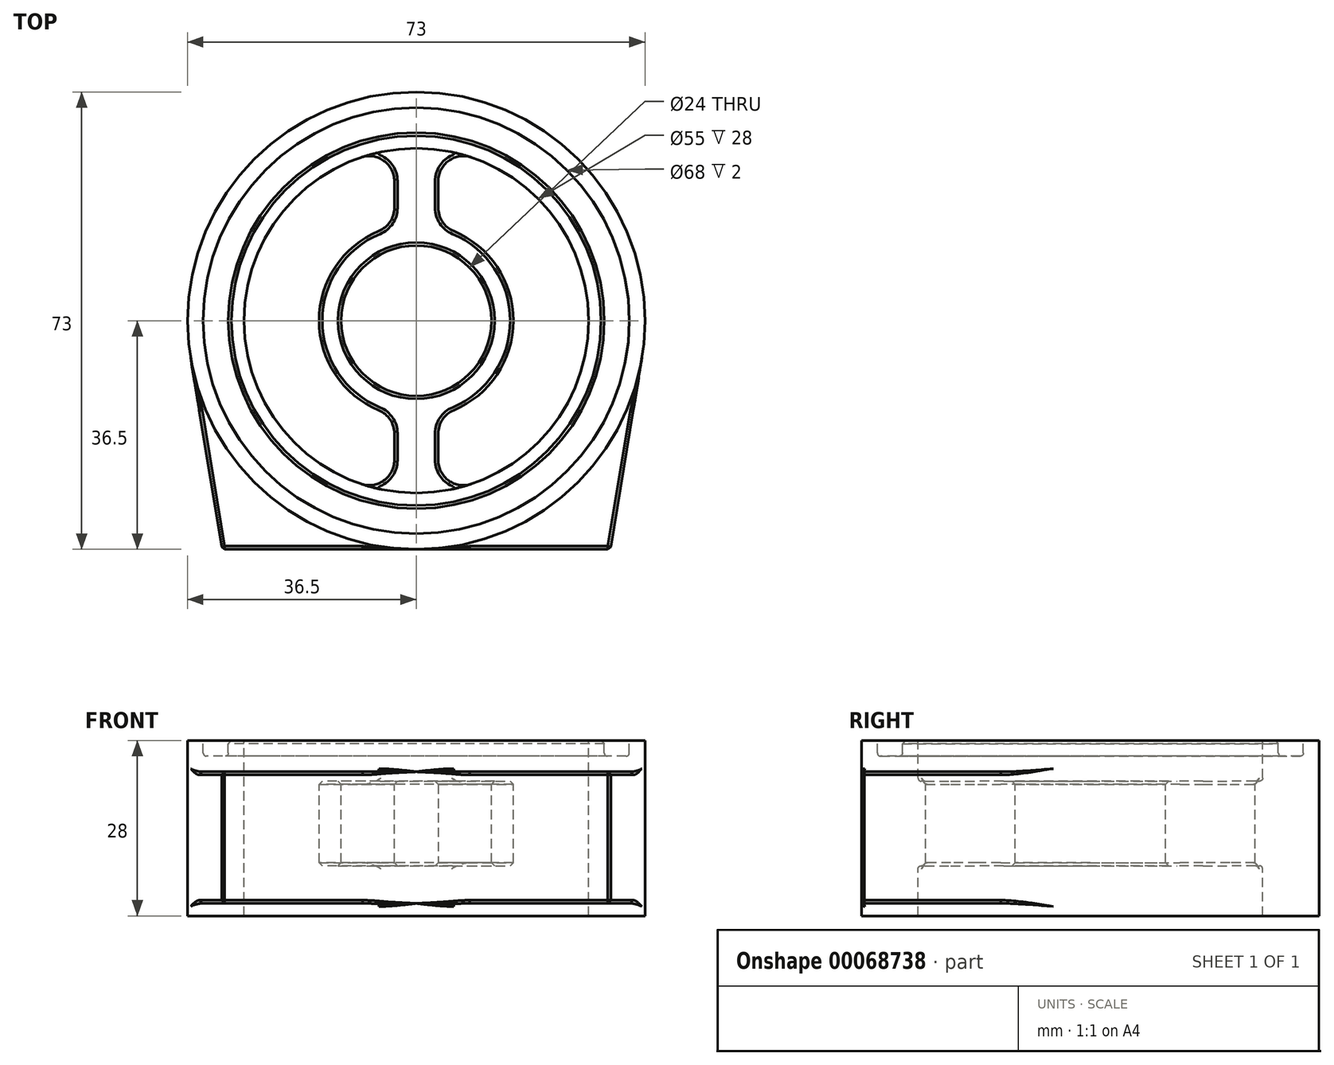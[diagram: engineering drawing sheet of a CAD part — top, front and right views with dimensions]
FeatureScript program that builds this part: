
annotation { "Feature Type Name" : "Feature", "Feature Type Description" : "" }
export const myFeature = defineFeature(function(context is Context, id is Id, definition is map)
    precondition{}
    {
        {
            var Q0;
            Q0=qCreatedBy(makeId("Top.planeOp"),FACE);
            var sketch = newSketch(context, id + "F0", { "sketchPlane" : qUnion([Q0])});
            skCircle(sketch, "E0", {"center": v(0, 0) * mm, "radius": 36.5 * mm});
            skLineSegment(sketch, "E1", {"start": v(-70.7, 0) * mm, "end": v(75.45, 0) * mm, "construction": true});
            skLineSegment(sketch, "E2", {"start": v(0, 57.55) * mm, "end": v(0, -65.93) * mm, "construction": true});
            skLineSegment(sketch, "E3", {"start": v(-31, -36.5) * mm, "end": v(31, -36.5) * mm});
            skLineSegment(sketch, "E4", {"start": v(31, -36.5) * mm, "end": v(36.02, -5.9) * mm});
            skLineSegment(sketch, "E5", {"start": v(-31, -36.5) * mm, "end": v(-36.02, -5.9) * mm});
            skSolve(sketch);
        }
        {
            var Q0;
            Q0 = qSketchRegion(id + "F0", true);
            extrude(context, id + "F1", {"entities" : qUnion([Q0]), "endBound" : BoundingType.SYMMETRIC, "depth" : 28 * mm});
        }
        {
            var Q0;
            Q0=makeQuery(id+"F1.opExtrude","CAP_FACE",FACE,{"disambiguationData":[OSD([sQuery(id+"F0.wireOp",EDGE,"E0"),sQuery(id+"F0.wireOp",EDGE,"E3"),sQuery(id+"F0.wireOp",EDGE,"E4"),sQuery(id+"F0.wireOp",EDGE,"E5")])],"isStart":false});
            var sketch = newSketch(context, id + "F2", { "sketchPlane" : qUnion([Q0])});
            skLineSegment(sketch, "E6", {"start": v(-31, -36.5) * mm, "end": v(-36.02, -5.9) * mm});
            skLineSegment(sketch, "E7", {"start": v(31, -36.5) * mm, "end": v(36.02, -5.9) * mm});
            skLineSegment(sketch, "E8", {"start": v(-31, -36.5) * mm, "end": v(31, -36.5) * mm});
            skArc(sketch, "E9", {"start": v(-36.02, -5.9) * mm, "mid": v(0, -36.5) * mm, "end": v(36.02, -5.9) * mm});
            skSolve(sketch);
        }
        {
            var Q0;
            Q0 = qSketchRegion(id + "F2", true);
            extrude(context, id + "F3", {"entities" : qUnion([Q0]), "operationType" : NewBodyOperationType.REMOVE, "oppositeDirection" : true, "depth" : 5 * mm});
        }
        {
            var Q0;
            Q0=makeQuery(id+"F1.opExtrude","CAP_FACE",FACE,{"disambiguationData":[OSD([sQuery(id+"F0.wireOp",EDGE,"E0"),sQuery(id+"F0.wireOp",EDGE,"E3"),sQuery(id+"F0.wireOp",EDGE,"E4"),sQuery(id+"F0.wireOp",EDGE,"E5")])],"isStart":true});
            var sketch = newSketch(context, id + "F4", { "sketchPlane" : qUnion([Q0])});
            skArc(sketch, "E10", {"start": v(36.02, 5.9) * mm, "mid": v(0, 36.5) * mm, "end": v(-36.02, 5.9) * mm});
            skLineSegment(sketch, "E11", {"start": v(-31, 36.5) * mm, "end": v(31, 36.5) * mm});
            skLineSegment(sketch, "E12", {"start": v(31, 36.5) * mm, "end": v(36.02, 5.9) * mm});
            skLineSegment(sketch, "E13", {"start": v(-31, 36.5) * mm, "end": v(-36.02, 5.9) * mm});
            skSolve(sketch);
        }
        {
            var Q0;
            Q0 = qSketchRegion(id + "F4", true);
            extrude(context, id + "F5", {"entities" : qUnion([Q0]), "operationType" : NewBodyOperationType.REMOVE, "oppositeDirection" : true, "depth" : 2 * mm});
        }
        {
            var Q0;
            Q0=makeQuery(id+"F1.opExtrude","CAP_FACE",FACE,{"disambiguationData":[OSD([sQuery(id+"F0.wireOp",EDGE,"E0"),sQuery(id+"F0.wireOp",EDGE,"E3"),sQuery(id+"F0.wireOp",EDGE,"E4"),sQuery(id+"F0.wireOp",EDGE,"E5")])],"isStart":false});
            var sketch = newSketch(context, id + "F6", { "sketchPlane" : qUnion([Q0])});
            skArc(sketch, "E14", {"start": v(-3.5, 27.28) * mm, "mid": v(-27.5, 0) * mm, "end": v(-3.5, -27.28) * mm});
            skArc(sketch, "E15", {"start": v(-3.5, 15.1) * mm, "mid": v(-15.5, 0) * mm, "end": v(-3.5, -15.1) * mm});
            skCircle(sketch, "E16", {"center": v(0, 0) * mm, "radius": 12 * mm});
            skLineSegment(sketch, "E17", {"start": v(-3.5, 27.28) * mm, "end": v(-3.5, 15.1) * mm});
            skLineSegment(sketch, "E18", {"start": v(3.5, 27.28) * mm, "end": v(3.5, 15.1) * mm});
            skLineSegment(sketch, "E19", {"start": v(-3.5, -15.1) * mm, "end": v(-3.5, -27.28) * mm});
            skLineSegment(sketch, "E20", {"start": v(3.5, -15.1) * mm, "end": v(3.5, -27.28) * mm});
            skArc(sketch, "E21.trimOffspring", {"start": v(3.5, -15.1) * mm, "mid": v(15.5, 0) * mm, "end": v(3.5, 15.1) * mm});
            skArc(sketch, "E22.trimOffspring", {"start": v(3.5, -27.28) * mm, "mid": v(27.5, 0) * mm, "end": v(3.5, 27.28) * mm});
            skSolve(sketch);
        }
        {
            var Q0;
            Q0 = qSketchRegion(id + "F6", true);
            extrude(context, id + "F7", {"entities" : qUnion([Q0]), "operationType" : NewBodyOperationType.REMOVE, "endBound" : BoundingType.THROUGH_ALL, "oppositeDirection" : true, "depth" : 25 * mm});
        }
        {
            var Q0;
            Q0=makeQuery(id+"F7.boolean.opBoolean","COPY",EDGE,{"derivedFrom":makeQuery(id+"F7.opExtrude","SWEPT_EDGE",EDGE,{"disambiguationData":[OSD([sQuery(id+"F6.wireOp",EDGE,"E18"),sQuery(id+"F6.wireOp",EDGE,"E22.trimOffspring")])]})});
            var Q1;
            Q1=makeQuery(id+"F7.boolean.opBoolean","COPY",EDGE,{"derivedFrom":makeQuery(id+"F7.opExtrude","SWEPT_EDGE",EDGE,{"disambiguationData":[OSD([sQuery(id+"F6.wireOp",EDGE,"E18"),sQuery(id+"F6.wireOp",EDGE,"E21.trimOffspring")])]})});
            var Q2;
            Q2=makeQuery(id+"F7.boolean.opBoolean","COPY",EDGE,{"derivedFrom":makeQuery(id+"F7.opExtrude","SWEPT_EDGE",EDGE,{"disambiguationData":[OSD([sQuery(id+"F6.wireOp",EDGE,"E20"),sQuery(id+"F6.wireOp",EDGE,"E21.trimOffspring")])]})});
            var Q3;
            Q3=makeQuery(id+"F7.boolean.opBoolean","COPY",EDGE,{"derivedFrom":makeQuery(id+"F7.opExtrude","SWEPT_EDGE",EDGE,{"disambiguationData":[OSD([sQuery(id+"F6.wireOp",EDGE,"E20"),sQuery(id+"F6.wireOp",EDGE,"E22.trimOffspring")])]})});
            var Q4;
            Q4=makeQuery(id+"F7.boolean.opBoolean","COPY",EDGE,{"derivedFrom":makeQuery(id+"F7.opExtrude","SWEPT_EDGE",EDGE,{"disambiguationData":[OSD([sQuery(id+"F6.wireOp",EDGE,"E14"),sQuery(id+"F6.wireOp",EDGE,"E17")])]})});
            var Q5;
            Q5=makeQuery(id+"F7.boolean.opBoolean","COPY",EDGE,{"derivedFrom":makeQuery(id+"F7.opExtrude","SWEPT_EDGE",EDGE,{"disambiguationData":[OSD([sQuery(id+"F6.wireOp",EDGE,"E15"),sQuery(id+"F6.wireOp",EDGE,"E17")])]})});
            var Q6;
            Q6=makeQuery(id+"F7.boolean.opBoolean","COPY",EDGE,{"derivedFrom":makeQuery(id+"F7.opExtrude","SWEPT_EDGE",EDGE,{"disambiguationData":[OSD([sQuery(id+"F6.wireOp",EDGE,"E15"),sQuery(id+"F6.wireOp",EDGE,"E19")])]})});
            var Q7;
            Q7=makeQuery(id+"F7.boolean.opBoolean","COPY",EDGE,{"derivedFrom":makeQuery(id+"F7.opExtrude","SWEPT_EDGE",EDGE,{"disambiguationData":[OSD([sQuery(id+"F6.wireOp",EDGE,"E14"),sQuery(id+"F6.wireOp",EDGE,"E19")])]})});
            fillet(context, id + "F8", {"entities" : qUnion([Q0, Q1, Q2, Q3, Q4, Q5, Q6, Q7]), "radius" : 4 * mm, "tangentPropagation" : true, "allowEdgeOverflow" : false});
        }
        {
            var Q0;
            Q0=makeQuery(id+"F1.opExtrude","CAP_FACE",FACE,{"disambiguationData":[OSD([sQuery(id+"F0.wireOp",EDGE,"E0"),sQuery(id+"F0.wireOp",EDGE,"E3"),sQuery(id+"F0.wireOp",EDGE,"E4"),sQuery(id+"F0.wireOp",EDGE,"E5")])],"isStart":false});
            var sketch = newSketch(context, id + "F9", { "sketchPlane" : qUnion([Q0])});
            skCircle(sketch, "E23", {"center": v(0, 0) * mm, "radius": 27.5 * mm});
            skSolve(sketch);
        }
        {
            var Q0;
            Q0 = qSketchRegion(id + "F9", true);
            extrude(context, id + "F10", {"entities" : qUnion([Q0]), "operationType" : NewBodyOperationType.REMOVE, "oppositeDirection" : true, "depth" : 6.5 * mm});
        }
        {
            var Q0;
            Q0=makeQuery(id+"F1.opExtrude","CAP_FACE",FACE,{"disambiguationData":[OSD([sQuery(id+"F0.wireOp",EDGE,"E0"),sQuery(id+"F0.wireOp",EDGE,"E3"),sQuery(id+"F0.wireOp",EDGE,"E4"),sQuery(id+"F0.wireOp",EDGE,"E5")])],"isStart":true});
            var sketch = newSketch(context, id + "F11", { "sketchPlane" : qUnion([Q0])});
            skCircle(sketch, "E24", {"center": v(0, 0) * mm, "radius": 27.5 * mm});
            skSolve(sketch);
        }
        {
            var Q0;
            Q0 = qSketchRegion(id + "F11", true);
            extrude(context, id + "F12", {"entities" : qUnion([Q0]), "operationType" : NewBodyOperationType.REMOVE, "oppositeDirection" : true, "depth" : 8 * mm});
        }
        {
            var Q0;
            Q0=makeQuery(id+"F1.opExtrude","CAP_FACE",FACE,{"disambiguationData":[OSD([sQuery(id+"F0.wireOp",EDGE,"E0"),sQuery(id+"F0.wireOp",EDGE,"E3"),sQuery(id+"F0.wireOp",EDGE,"E4"),sQuery(id+"F0.wireOp",EDGE,"E5")])],"isStart":false});
            var sketch = newSketch(context, id + "F13", { "sketchPlane" : qUnion([Q0])});
            skCircle(sketch, "E25", {"center": v(0, 0) * mm, "radius": 30 * mm});
            skCircle(sketch, "E26", {"center": v(0, 0) * mm, "radius": 34 * mm});
            skSolve(sketch);
        }
        {
            var Q0;
            Q0 = qSketchRegion(id + "F13", true);
            extrude(context, id + "F14", {"entities" : qUnion([Q0]), "operationType" : NewBodyOperationType.REMOVE, "oppositeDirection" : true, "depth" : 2.5 * mm});
        }
        {
            var Q0;
            Q0=makeQuery(id+"F10.boolean.opBoolean","INTERSECT",EDGE,{"derivedFrom":[makeQuery(id+"F8.opFillet","BLEND_FACE",FACE,{"disambiguationData":[OSD([sQuery(id+"F6.wireOp",EDGE,"E18"),sQuery(id+"F6.wireOp",EDGE,"E22.trimOffspring")])]}),makeQuery(id+"F10.opExtrude","CAP_FACE",FACE,{"disambiguationData":[OSD([sQuery(id+"F9.wireOp",EDGE,"E23")])],"isStart":false})]});
            var Q1;
            Q1=makeQuery(id+"F10.boolean.opBoolean","INTERSECT",EDGE,{"derivedFrom":[makeQuery(id+"F7.boolean.opBoolean","COPY",FACE,{"derivedFrom":makeQuery(id+"F7.opExtrude","SWEPT_FACE",FACE,{"disambiguationData":[OSD([sQuery(id+"F6.wireOp",EDGE,"E18")])]})}),makeQuery(id+"F10.opExtrude","CAP_FACE",FACE,{"disambiguationData":[OSD([sQuery(id+"F9.wireOp",EDGE,"E23")])],"isStart":false})]});
            var Q2;
            Q2=makeQuery(id+"F10.boolean.opBoolean","INTERSECT",EDGE,{"derivedFrom":[makeQuery(id+"F8.opFillet","BLEND_FACE",FACE,{"disambiguationData":[OSD([sQuery(id+"F6.wireOp",EDGE,"E18"),sQuery(id+"F6.wireOp",EDGE,"E21.trimOffspring")])]}),makeQuery(id+"F10.opExtrude","CAP_FACE",FACE,{"disambiguationData":[OSD([sQuery(id+"F9.wireOp",EDGE,"E23")])],"isStart":false})]});
            var Q3;
            Q3=makeQuery(id+"F10.boolean.opBoolean","INTERSECT",EDGE,{"derivedFrom":[makeQuery(id+"F7.boolean.opBoolean","COPY",FACE,{"derivedFrom":makeQuery(id+"F7.opExtrude","SWEPT_FACE",FACE,{"disambiguationData":[OSD([sQuery(id+"F6.wireOp",EDGE,"E21.trimOffspring")])]})}),makeQuery(id+"F10.opExtrude","CAP_FACE",FACE,{"disambiguationData":[OSD([sQuery(id+"F9.wireOp",EDGE,"E23")])],"isStart":false})]});
            var Q4;
            Q4=makeQuery(id+"F10.boolean.opBoolean","INTERSECT",EDGE,{"derivedFrom":[makeQuery(id+"F8.opFillet","BLEND_FACE",FACE,{"disambiguationData":[OSD([sQuery(id+"F6.wireOp",EDGE,"E20"),sQuery(id+"F6.wireOp",EDGE,"E21.trimOffspring")])]}),makeQuery(id+"F10.opExtrude","CAP_FACE",FACE,{"disambiguationData":[OSD([sQuery(id+"F9.wireOp",EDGE,"E23")])],"isStart":false})]});
            var Q5;
            Q5=makeQuery(id+"F10.boolean.opBoolean","INTERSECT",EDGE,{"derivedFrom":[makeQuery(id+"F7.boolean.opBoolean","COPY",FACE,{"derivedFrom":makeQuery(id+"F7.opExtrude","SWEPT_FACE",FACE,{"disambiguationData":[OSD([sQuery(id+"F6.wireOp",EDGE,"E20")])]})}),makeQuery(id+"F10.opExtrude","CAP_FACE",FACE,{"disambiguationData":[OSD([sQuery(id+"F9.wireOp",EDGE,"E23")])],"isStart":false})]});
            var Q6;
            Q6=makeQuery(id+"F10.boolean.opBoolean","INTERSECT",EDGE,{"derivedFrom":[makeQuery(id+"F8.opFillet","BLEND_FACE",FACE,{"disambiguationData":[OSD([sQuery(id+"F6.wireOp",EDGE,"E20"),sQuery(id+"F6.wireOp",EDGE,"E22.trimOffspring")])]}),makeQuery(id+"F10.opExtrude","CAP_FACE",FACE,{"disambiguationData":[OSD([sQuery(id+"F9.wireOp",EDGE,"E23")])],"isStart":false})]});
            var Q7;
            Q7=makeQuery(id+"F10.boolean.opBoolean","INTERSECT",EDGE,{"derivedFrom":[makeQuery(id+"F8.opFillet","BLEND_FACE",FACE,{"disambiguationData":[OSD([sQuery(id+"F6.wireOp",EDGE,"E14"),sQuery(id+"F6.wireOp",EDGE,"E19")])]}),makeQuery(id+"F10.opExtrude","CAP_FACE",FACE,{"disambiguationData":[OSD([sQuery(id+"F9.wireOp",EDGE,"E23")])],"isStart":false})]});
            var Q8;
            Q8=makeQuery(id+"F10.boolean.opBoolean","INTERSECT",EDGE,{"derivedFrom":[makeQuery(id+"F7.boolean.opBoolean","COPY",FACE,{"derivedFrom":makeQuery(id+"F7.opExtrude","SWEPT_FACE",FACE,{"disambiguationData":[OSD([sQuery(id+"F6.wireOp",EDGE,"E19")])]})}),makeQuery(id+"F10.opExtrude","CAP_FACE",FACE,{"disambiguationData":[OSD([sQuery(id+"F9.wireOp",EDGE,"E23")])],"isStart":false})]});
            var Q9;
            Q9=makeQuery(id+"F10.boolean.opBoolean","INTERSECT",EDGE,{"derivedFrom":[makeQuery(id+"F8.opFillet","BLEND_FACE",FACE,{"disambiguationData":[OSD([sQuery(id+"F6.wireOp",EDGE,"E15"),sQuery(id+"F6.wireOp",EDGE,"E19")])]}),makeQuery(id+"F10.opExtrude","CAP_FACE",FACE,{"disambiguationData":[OSD([sQuery(id+"F9.wireOp",EDGE,"E23")])],"isStart":false})]});
            var Q10;
            Q10=makeQuery(id+"F10.boolean.opBoolean","INTERSECT",EDGE,{"derivedFrom":[makeQuery(id+"F7.boolean.opBoolean","COPY",FACE,{"derivedFrom":makeQuery(id+"F7.opExtrude","SWEPT_FACE",FACE,{"disambiguationData":[OSD([sQuery(id+"F6.wireOp",EDGE,"E15")])]})}),makeQuery(id+"F10.opExtrude","CAP_FACE",FACE,{"disambiguationData":[OSD([sQuery(id+"F9.wireOp",EDGE,"E23")])],"isStart":false})]});
            var Q11;
            Q11=makeQuery(id+"F10.boolean.opBoolean","INTERSECT",EDGE,{"derivedFrom":[makeQuery(id+"F8.opFillet","BLEND_FACE",FACE,{"disambiguationData":[OSD([sQuery(id+"F6.wireOp",EDGE,"E15"),sQuery(id+"F6.wireOp",EDGE,"E17")])]}),makeQuery(id+"F10.opExtrude","CAP_FACE",FACE,{"disambiguationData":[OSD([sQuery(id+"F9.wireOp",EDGE,"E23")])],"isStart":false})]});
            var Q12;
            Q12=makeQuery(id+"F10.boolean.opBoolean","INTERSECT",EDGE,{"derivedFrom":[makeQuery(id+"F7.boolean.opBoolean","COPY",FACE,{"derivedFrom":makeQuery(id+"F7.opExtrude","SWEPT_FACE",FACE,{"disambiguationData":[OSD([sQuery(id+"F6.wireOp",EDGE,"E17")])]})}),makeQuery(id+"F10.opExtrude","CAP_FACE",FACE,{"disambiguationData":[OSD([sQuery(id+"F9.wireOp",EDGE,"E23")])],"isStart":false})]});
            var Q13;
            Q13=makeQuery(id+"F10.boolean.opBoolean","INTERSECT",EDGE,{"derivedFrom":[makeQuery(id+"F8.opFillet","BLEND_FACE",FACE,{"disambiguationData":[OSD([sQuery(id+"F6.wireOp",EDGE,"E14"),sQuery(id+"F6.wireOp",EDGE,"E17")])]}),makeQuery(id+"F10.opExtrude","CAP_FACE",FACE,{"disambiguationData":[OSD([sQuery(id+"F9.wireOp",EDGE,"E23")])],"isStart":false})]});
            var Q14;
            Q14=makeQuery(id+"F10.boolean.opBoolean","INTERSECT",EDGE,{"derivedFrom":[makeQuery(id+"F7.boolean.opBoolean","COPY",FACE,{"derivedFrom":makeQuery(id+"F7.opExtrude","SWEPT_FACE",FACE,{"disambiguationData":[OSD([sQuery(id+"F6.wireOp",EDGE,"E16")])]})}),makeQuery(id+"F10.opExtrude","CAP_FACE",FACE,{"disambiguationData":[OSD([sQuery(id+"F9.wireOp",EDGE,"E23")])],"isStart":false})]});
            var Q15;
            Q15=makeQuery(id+"F12.boolean.opBoolean","INTERSECT",EDGE,{"derivedFrom":[makeQuery(id+"F8.opFillet","BLEND_FACE",FACE,{"disambiguationData":[OSD([sQuery(id+"F6.wireOp",EDGE,"E18"),sQuery(id+"F6.wireOp",EDGE,"E22.trimOffspring")])]}),makeQuery(id+"F12.opExtrude","CAP_FACE",FACE,{"disambiguationData":[OSD([sQuery(id+"F11.wireOp",EDGE,"E24")])],"isStart":false})]});
            var Q16;
            Q16=makeQuery(id+"F12.boolean.opBoolean","INTERSECT",EDGE,{"derivedFrom":[makeQuery(id+"F7.boolean.opBoolean","COPY",FACE,{"derivedFrom":makeQuery(id+"F7.opExtrude","SWEPT_FACE",FACE,{"disambiguationData":[OSD([sQuery(id+"F6.wireOp",EDGE,"E18")])]})}),makeQuery(id+"F12.opExtrude","CAP_FACE",FACE,{"disambiguationData":[OSD([sQuery(id+"F11.wireOp",EDGE,"E24")])],"isStart":false})]});
            var Q17;
            Q17=makeQuery(id+"F12.boolean.opBoolean","INTERSECT",EDGE,{"derivedFrom":[makeQuery(id+"F8.opFillet","BLEND_FACE",FACE,{"disambiguationData":[OSD([sQuery(id+"F6.wireOp",EDGE,"E18"),sQuery(id+"F6.wireOp",EDGE,"E21.trimOffspring")])]}),makeQuery(id+"F12.opExtrude","CAP_FACE",FACE,{"disambiguationData":[OSD([sQuery(id+"F11.wireOp",EDGE,"E24")])],"isStart":false})]});
            var Q18;
            Q18=makeQuery(id+"F12.boolean.opBoolean","INTERSECT",EDGE,{"derivedFrom":[makeQuery(id+"F7.boolean.opBoolean","COPY",FACE,{"derivedFrom":makeQuery(id+"F7.opExtrude","SWEPT_FACE",FACE,{"disambiguationData":[OSD([sQuery(id+"F6.wireOp",EDGE,"E21.trimOffspring")])]})}),makeQuery(id+"F12.opExtrude","CAP_FACE",FACE,{"disambiguationData":[OSD([sQuery(id+"F11.wireOp",EDGE,"E24")])],"isStart":false})]});
            var Q19;
            Q19=makeQuery(id+"F12.boolean.opBoolean","INTERSECT",EDGE,{"derivedFrom":[makeQuery(id+"F8.opFillet","BLEND_FACE",FACE,{"disambiguationData":[OSD([sQuery(id+"F6.wireOp",EDGE,"E20"),sQuery(id+"F6.wireOp",EDGE,"E21.trimOffspring")])]}),makeQuery(id+"F12.opExtrude","CAP_FACE",FACE,{"disambiguationData":[OSD([sQuery(id+"F11.wireOp",EDGE,"E24")])],"isStart":false})]});
            var Q20;
            Q20=makeQuery(id+"F12.boolean.opBoolean","INTERSECT",EDGE,{"derivedFrom":[makeQuery(id+"F7.boolean.opBoolean","COPY",FACE,{"derivedFrom":makeQuery(id+"F7.opExtrude","SWEPT_FACE",FACE,{"disambiguationData":[OSD([sQuery(id+"F6.wireOp",EDGE,"E20")])]})}),makeQuery(id+"F12.opExtrude","CAP_FACE",FACE,{"disambiguationData":[OSD([sQuery(id+"F11.wireOp",EDGE,"E24")])],"isStart":false})]});
            var Q21;
            Q21=makeQuery(id+"F12.boolean.opBoolean","INTERSECT",EDGE,{"derivedFrom":[makeQuery(id+"F8.opFillet","BLEND_FACE",FACE,{"disambiguationData":[OSD([sQuery(id+"F6.wireOp",EDGE,"E20"),sQuery(id+"F6.wireOp",EDGE,"E22.trimOffspring")])]}),makeQuery(id+"F12.opExtrude","CAP_FACE",FACE,{"disambiguationData":[OSD([sQuery(id+"F11.wireOp",EDGE,"E24")])],"isStart":false})]});
            var Q22;
            Q22=makeQuery(id+"F12.boolean.opBoolean","INTERSECT",EDGE,{"derivedFrom":[makeQuery(id+"F7.boolean.opBoolean","COPY",FACE,{"derivedFrom":makeQuery(id+"F7.opExtrude","SWEPT_FACE",FACE,{"disambiguationData":[OSD([sQuery(id+"F6.wireOp",EDGE,"E16")])]})}),makeQuery(id+"F12.opExtrude","CAP_FACE",FACE,{"disambiguationData":[OSD([sQuery(id+"F11.wireOp",EDGE,"E24")])],"isStart":false})]});
            var Q23;
            Q23=makeQuery(id+"F12.boolean.opBoolean","INTERSECT",EDGE,{"derivedFrom":[makeQuery(id+"F8.opFillet","BLEND_FACE",FACE,{"disambiguationData":[OSD([sQuery(id+"F6.wireOp",EDGE,"E14"),sQuery(id+"F6.wireOp",EDGE,"E17")])]}),makeQuery(id+"F12.opExtrude","CAP_FACE",FACE,{"disambiguationData":[OSD([sQuery(id+"F11.wireOp",EDGE,"E24")])],"isStart":false})]});
            var Q24;
            Q24=makeQuery(id+"F12.boolean.opBoolean","INTERSECT",EDGE,{"derivedFrom":[makeQuery(id+"F7.boolean.opBoolean","COPY",FACE,{"derivedFrom":makeQuery(id+"F7.opExtrude","SWEPT_FACE",FACE,{"disambiguationData":[OSD([sQuery(id+"F6.wireOp",EDGE,"E17")])]})}),makeQuery(id+"F12.opExtrude","CAP_FACE",FACE,{"disambiguationData":[OSD([sQuery(id+"F11.wireOp",EDGE,"E24")])],"isStart":false})]});
            var Q25;
            Q25=makeQuery(id+"F12.boolean.opBoolean","INTERSECT",EDGE,{"derivedFrom":[makeQuery(id+"F8.opFillet","BLEND_FACE",FACE,{"disambiguationData":[OSD([sQuery(id+"F6.wireOp",EDGE,"E15"),sQuery(id+"F6.wireOp",EDGE,"E17")])]}),makeQuery(id+"F12.opExtrude","CAP_FACE",FACE,{"disambiguationData":[OSD([sQuery(id+"F11.wireOp",EDGE,"E24")])],"isStart":false})]});
            var Q26;
            Q26=makeQuery(id+"F12.boolean.opBoolean","INTERSECT",EDGE,{"derivedFrom":[makeQuery(id+"F7.boolean.opBoolean","COPY",FACE,{"derivedFrom":makeQuery(id+"F7.opExtrude","SWEPT_FACE",FACE,{"disambiguationData":[OSD([sQuery(id+"F6.wireOp",EDGE,"E15")])]})}),makeQuery(id+"F12.opExtrude","CAP_FACE",FACE,{"disambiguationData":[OSD([sQuery(id+"F11.wireOp",EDGE,"E24")])],"isStart":false})]});
            var Q27;
            Q27=makeQuery(id+"F12.boolean.opBoolean","INTERSECT",EDGE,{"derivedFrom":[makeQuery(id+"F8.opFillet","BLEND_FACE",FACE,{"disambiguationData":[OSD([sQuery(id+"F6.wireOp",EDGE,"E15"),sQuery(id+"F6.wireOp",EDGE,"E19")])]}),makeQuery(id+"F12.opExtrude","CAP_FACE",FACE,{"disambiguationData":[OSD([sQuery(id+"F11.wireOp",EDGE,"E24")])],"isStart":false})]});
            var Q28;
            Q28=makeQuery(id+"F12.boolean.opBoolean","INTERSECT",EDGE,{"derivedFrom":[makeQuery(id+"F7.boolean.opBoolean","COPY",FACE,{"derivedFrom":makeQuery(id+"F7.opExtrude","SWEPT_FACE",FACE,{"disambiguationData":[OSD([sQuery(id+"F6.wireOp",EDGE,"E19")])]})}),makeQuery(id+"F12.opExtrude","CAP_FACE",FACE,{"disambiguationData":[OSD([sQuery(id+"F11.wireOp",EDGE,"E24")])],"isStart":false})]});
            var Q29;
            Q29=makeQuery(id+"F12.boolean.opBoolean","INTERSECT",EDGE,{"derivedFrom":[makeQuery(id+"F8.opFillet","BLEND_FACE",FACE,{"disambiguationData":[OSD([sQuery(id+"F6.wireOp",EDGE,"E14"),sQuery(id+"F6.wireOp",EDGE,"E19")])]}),makeQuery(id+"F12.opExtrude","CAP_FACE",FACE,{"disambiguationData":[OSD([sQuery(id+"F11.wireOp",EDGE,"E24")])],"isStart":false})]});
            var Q30;
            {var subQ0=makeQuery(id+"F1.opExtrude","CAP_FACE",FACE,{"disambiguationData":[OSD([sQuery(id+"F0.wireOp",EDGE,"E0"),sQuery(id+"F0.wireOp",EDGE,"E3"),sQuery(id+"F0.wireOp",EDGE,"E4"),sQuery(id+"F0.wireOp",EDGE,"E5")])],"isStart":true});Q30=makeQuery(id+"F12.boolean.opBoolean","MERGE",EDGE,{"derivedFrom":[makeQuery(id+"F7.boolean.opBoolean","INTERSECT",EDGE,{"derivedFrom":[subQ0,makeQuery(id+"F7.opExtrude","SWEPT_FACE",FACE,{"disambiguationData":[OSD([sQuery(id+"F6.wireOp",EDGE,"E14")])]})]}),makeQuery(id+"F7.boolean.opBoolean","INTERSECT",EDGE,{"derivedFrom":[subQ0,makeQuery(id+"F7.opExtrude","SWEPT_FACE",FACE,{"disambiguationData":[OSD([sQuery(id+"F6.wireOp",EDGE,"E22.trimOffspring")])]})]}),makeQuery(id+"F12.opExtrude","CAP_EDGE",EDGE,{"disambiguationData":[OSD([sQuery(id+"F11.wireOp",EDGE,"E24")])],"isStart":true})]});}
            var Q31;
            {var subQ0=sQuery(id+"F4.wireOp",EDGE,"E10");var subQ1=makeQuery(id+"F1.opExtrude","CAP_EDGE",EDGE,{"disambiguationData":[OSD([sQuery(id+"F0.wireOp",EDGE,"E0")])],"isStart":true});var subQ2=makeQuery(id+"F4.imprint","INTERSECT",VERTEX,{"derivedFrom":[subQ0,sQuery(id+"F4.wireOp",EDGE,"E11")]});Q31=makeQuery(id+"F5.boolean.opBoolean","MERGE",EDGE,{"derivedFrom":[subQ1,makeQuery(id+"F5.opExtrude","CAP_EDGE",EDGE,{"disambiguationData":[OSD([subQ0]),TDD([makeQuery(id+"F4.imprint","IMPRINT",EDGE,{"disambiguationData":[TD([[subQ2,1.0]])],"derivedFrom":subQ0})])],"isStart":true}),makeQuery(id+"F5.opExtrude","CAP_EDGE",EDGE,{"disambiguationData":[OSD([subQ0]),TDD([makeQuery(id+"F4.imprint","IMPRINT",EDGE,{"disambiguationData":[TD([[subQ2,-1.0]])],"derivedFrom":subQ0})])],"isStart":true})]});}
            var Q32;
            Q32=makeQuery(id+"F10.boolean.opBoolean","MERGE",EDGE,{"derivedFrom":[makeQuery(id+"F7.boolean.opBoolean","COPY",EDGE,{"derivedFrom":makeQuery(id+"F7.opExtrude","CAP_EDGE",EDGE,{"disambiguationData":[OSD([sQuery(id+"F6.wireOp",EDGE,"E14")])],"isStart":true})}),makeQuery(id+"F7.boolean.opBoolean","COPY",EDGE,{"derivedFrom":makeQuery(id+"F7.opExtrude","CAP_EDGE",EDGE,{"disambiguationData":[OSD([sQuery(id+"F6.wireOp",EDGE,"E22.trimOffspring")])],"isStart":true})}),makeQuery(id+"F10.opExtrude","CAP_EDGE",EDGE,{"disambiguationData":[OSD([sQuery(id+"F9.wireOp",EDGE,"E23")])],"isStart":true})]});
            var Q33;
            Q33=makeQuery(id+"F14.boolean.opBoolean","COPY",EDGE,{"derivedFrom":makeQuery(id+"F14.opExtrude","CAP_EDGE",EDGE,{"disambiguationData":[OSD([sQuery(id+"F13.wireOp",EDGE,"E25")])],"isStart":true})});
            var Q34;
            Q34=makeQuery(id+"F14.boolean.opBoolean","COPY",EDGE,{"derivedFrom":makeQuery(id+"F14.opExtrude","CAP_EDGE",EDGE,{"disambiguationData":[OSD([sQuery(id+"F13.wireOp",EDGE,"E26")])],"isStart":true})});
            var Q35;
            {var subQ0=sQuery(id+"F2.wireOp",EDGE,"E9");var subQ1=makeQuery(id+"F1.opExtrude","CAP_EDGE",EDGE,{"disambiguationData":[OSD([sQuery(id+"F0.wireOp",EDGE,"E0")])],"isStart":false});var subQ2=makeQuery(id+"F2.imprint","INTERSECT",VERTEX,{"derivedFrom":[sQuery(id+"F2.wireOp",EDGE,"E8"),subQ0]});Q35=makeQuery(id+"F3.boolean.opBoolean","MERGE",EDGE,{"derivedFrom":[subQ1,makeQuery(id+"F3.opExtrude","CAP_EDGE",EDGE,{"disambiguationData":[OSD([subQ0]),TDD([makeQuery(id+"F2.imprint","IMPRINT",EDGE,{"disambiguationData":[TD([[subQ2,1.0]])],"derivedFrom":subQ0})])],"isStart":true}),makeQuery(id+"F3.opExtrude","CAP_EDGE",EDGE,{"disambiguationData":[OSD([subQ0]),TDD([makeQuery(id+"F2.imprint","IMPRINT",EDGE,{"disambiguationData":[TD([[subQ2,-1.0]])],"derivedFrom":subQ0})])],"isStart":true})]});}
            chamfer(context, id + "F15", {"entities" : qUnion([Q0, Q1, Q2, Q3, Q4, Q5, Q6, Q7, Q8, Q9, Q10, Q11, Q12, Q13, Q14, Q15, Q16, Q17, Q18, Q19, Q20, Q21, Q22, Q23, Q24, Q25, Q26, Q27, Q28, Q29, Q30, Q31, Q32, Q33, Q34, Q35]), "width" : 0.5 * mm, "tangentPropagation" : true});
        }
        {
            var Q0;
            Q0=makeQuery(id+"F10.boolean.opBoolean","COPY",EDGE,{"disambiguationData":[OD(1.0)],"derivedFrom":makeQuery(id+"F10.opExtrude","CAP_EDGE",EDGE,{"disambiguationData":[OSD([sQuery(id+"F9.wireOp",EDGE,"E23")])],"isStart":false})});
            var Q1;
            Q1=makeQuery(id+"F10.boolean.opBoolean","COPY",EDGE,{"disambiguationData":[OD(0.0)],"derivedFrom":makeQuery(id+"F10.opExtrude","CAP_EDGE",EDGE,{"disambiguationData":[OSD([sQuery(id+"F9.wireOp",EDGE,"E23")])],"isStart":false})});
            var Q2;
            Q2=makeQuery(id+"F12.boolean.opBoolean","COPY",EDGE,{"disambiguationData":[OD(1.0)],"derivedFrom":makeQuery(id+"F12.opExtrude","CAP_EDGE",EDGE,{"disambiguationData":[OSD([sQuery(id+"F11.wireOp",EDGE,"E24")])],"isStart":false})});
            var Q3;
            Q3=makeQuery(id+"F12.boolean.opBoolean","COPY",EDGE,{"disambiguationData":[OD(0.0)],"derivedFrom":makeQuery(id+"F12.opExtrude","CAP_EDGE",EDGE,{"disambiguationData":[OSD([sQuery(id+"F11.wireOp",EDGE,"E24")])],"isStart":false})});
            var Q4;
            Q4=makeQuery(id+"F14.boolean.opBoolean","COPY",EDGE,{"derivedFrom":makeQuery(id+"F14.opExtrude","CAP_EDGE",EDGE,{"disambiguationData":[OSD([sQuery(id+"F13.wireOp",EDGE,"E26")])],"isStart":false})});
            var Q5;
            Q5=makeQuery(id+"F14.boolean.opBoolean","COPY",EDGE,{"derivedFrom":makeQuery(id+"F14.opExtrude","CAP_EDGE",EDGE,{"disambiguationData":[OSD([sQuery(id+"F13.wireOp",EDGE,"E25")])],"isStart":false})});
            var Q6;
            {var subQ0=sQuery(id+"F2.wireOp",EDGE,"E9");Q6=makeQuery(id+"F3.boolean.opBoolean","COPY",EDGE,{"derivedFrom":makeQuery(id+"F3.opExtrude","CAP_EDGE",EDGE,{"disambiguationData":[OSD([subQ0]),TDD([makeQuery(id+"F2.imprint","IMPRINT",EDGE,{"disambiguationData":[TD([[makeQuery(id+"F2.imprint","INTERSECT",VERTEX,{"derivedFrom":[sQuery(id+"F2.wireOp",EDGE,"E8"),subQ0]}),1.0]])],"derivedFrom":subQ0})])],"isStart":false})});}
            var Q7;
            {var subQ0=sQuery(id+"F2.wireOp",EDGE,"E9");Q7=makeQuery(id+"F3.boolean.opBoolean","COPY",EDGE,{"derivedFrom":makeQuery(id+"F3.opExtrude","CAP_EDGE",EDGE,{"disambiguationData":[OSD([subQ0]),TDD([makeQuery(id+"F2.imprint","IMPRINT",EDGE,{"disambiguationData":[TD([[makeQuery(id+"F2.imprint","INTERSECT",VERTEX,{"derivedFrom":[sQuery(id+"F2.wireOp",EDGE,"E8"),subQ0]}),-1.0]])],"derivedFrom":subQ0})])],"isStart":false})});}
            var Q8;
            {var subQ0=sQuery(id+"F4.wireOp",EDGE,"E10");Q8=makeQuery(id+"F5.boolean.opBoolean","COPY",EDGE,{"derivedFrom":makeQuery(id+"F5.opExtrude","CAP_EDGE",EDGE,{"disambiguationData":[OSD([subQ0]),TDD([makeQuery(id+"F4.imprint","IMPRINT",EDGE,{"disambiguationData":[TD([[makeQuery(id+"F4.imprint","INTERSECT",VERTEX,{"derivedFrom":[subQ0,sQuery(id+"F4.wireOp",EDGE,"E11")]}),-1.0]])],"derivedFrom":subQ0})])],"isStart":false})});}
            var Q9;
            {var subQ0=sQuery(id+"F4.wireOp",EDGE,"E10");Q9=makeQuery(id+"F5.boolean.opBoolean","COPY",EDGE,{"derivedFrom":makeQuery(id+"F5.opExtrude","CAP_EDGE",EDGE,{"disambiguationData":[OSD([subQ0]),TDD([makeQuery(id+"F4.imprint","IMPRINT",EDGE,{"disambiguationData":[TD([[makeQuery(id+"F4.imprint","INTERSECT",VERTEX,{"derivedFrom":[subQ0,sQuery(id+"F4.wireOp",EDGE,"E11")]}),1.0]])],"derivedFrom":subQ0})])],"isStart":false})});}
            fillet(context, id + "F16", {"entities" : qUnion([Q0, Q1, Q2, Q3, Q4, Q5, Q6, Q7, Q8, Q9]), "radius" : 0.5 * mm, "tangentPropagation" : true, "allowEdgeOverflow" : false});
        }
        {
            var Q0;
            Q0=makeQuery(id+"F1.opExtrude","SWEPT_FACE",FACE,{"disambiguationData":[OSD([sQuery(id+"F0.wireOp",EDGE,"E3")])]});
            var Q1;
            Q1=makeQuery(id+"F1.opExtrude","SWEPT_FACE",FACE,{"disambiguationData":[OSD([sQuery(id+"F0.wireOp",EDGE,"E4")])]});
            var Q2;
            Q2=makeQuery(id+"F1.opExtrude","SWEPT_FACE",FACE,{"disambiguationData":[OSD([sQuery(id+"F0.wireOp",EDGE,"E5")])]});
            chamfer(context, id + "F17", {"entities" : qUnion([Q0, Q1, Q2]), "width" : 0.5 * mm, "tangentPropagation" : true});
        }
    });
